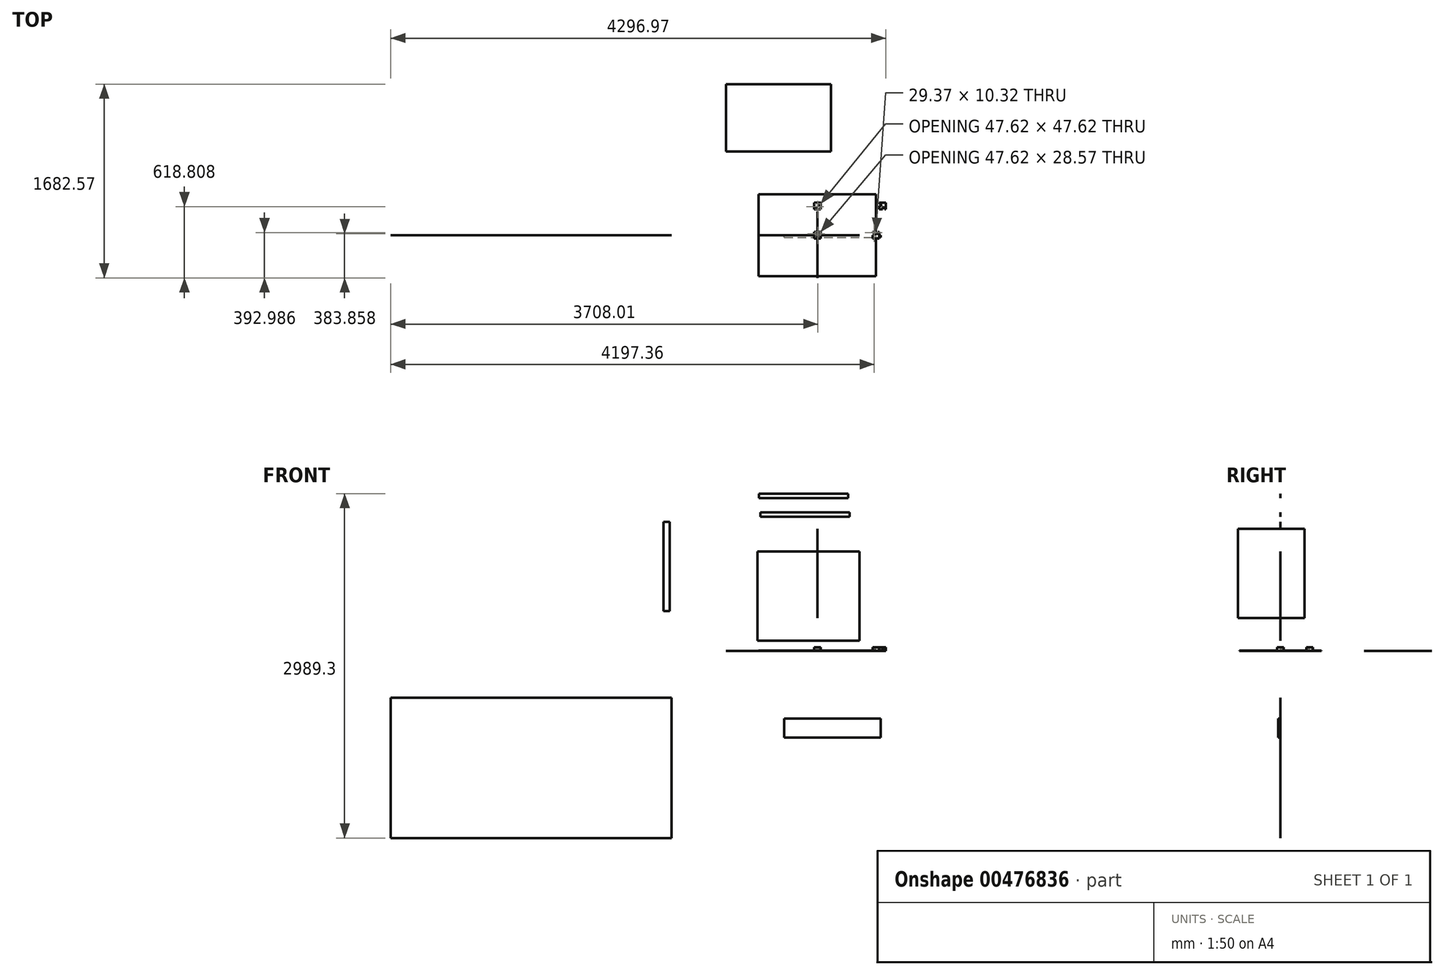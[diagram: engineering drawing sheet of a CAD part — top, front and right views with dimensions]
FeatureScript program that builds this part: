
annotation { "Feature Type Name" : "Feature", "Feature Type Description" : "" }
export const myFeature = defineFeature(function(context is Context, id is Id, definition is map)
    precondition{}
    {
        {
            assignVariable(context, id + "F0", {"name" : "h_total", "anyValue" : 36});
        }
        {
            assignVariable(context, id + "F1", {"name" : "h_caster", "anyValue" : 4});
        }
        {
            assignVariable(context, id + "F2", {"name" : "t_panel", "anyValue" : 0.72});
        }
        {
            assignVariable(context, id + "F3", {"name" : "t_top", "anyValue" : 1.5});
        }
        {
            assignVariable(context, id + "F4", {"name" : "h_panel", "anyValue" : getVariable(context, 'h_total') - getVariable(context, 'h_caster') - getVariable(context, 't_top')});
        }
        {
            var Q0;
            Q0=qCreatedBy(makeId("Top.planeOp"),FACE);
            var sketch = newSketch(context, id + "F5", { "sketchPlane" : qUnion([Q0])});
            skLineSegment(sketch, "E0.bottom", {"start": v(509.59, -355.6) * mm, "end": v(-509.59, -355.6) * mm});
            skLineSegment(sketch, "E0.top", {"start": v(509.59, 355.6) * mm, "end": v(-509.59, 355.6) * mm});
            skLineSegment(sketch, "E0.left", {"start": v(509.59, -355.6) * mm, "end": v(509.59, 355.6) * mm});
            skLineSegment(sketch, "E0.right", {"start": v(-509.59, -355.6) * mm, "end": v(-509.59, 355.6) * mm});
            skPoint(sketch, "E0.middle", {"position": v(0, 0) * mm});
            skSolve(sketch);
        }
        {
            var Q0;
            Q0=makeQuery(id+"F5.imprint","IMPRINT",FACE,{"disambiguationData":[TD([[makeQuery(id+"F5.imprint","IMPRINT",EDGE,{"derivedFrom":sQuery(id+"F5.wireOp",EDGE,"E0.bottom")}),-1.0]])]});
            extrude(context, id + "F6", {"entities" : qUnion([Q0]), "depth" : (getVariable(context, 't_top')) * mm});
        }
        {
            var Q0;
            Q0=qCreatedBy(makeId("Top.planeOp"),FACE);
            var sketch = newSketch(context, id + "F7", { "sketchPlane" : qUnion([Q0])});
            skLineSegment(sketch, "E1.bottom", {"start": v(-28.57, 28.58) * mm, "end": v(28.58, 28.58) * mm});
            skLineSegment(sketch, "E1.top", {"start": v(-28.58, -28.58) * mm, "end": v(28.58, -28.58) * mm});
            skLineSegment(sketch, "E1.left", {"start": v(-28.57, 28.58) * mm, "end": v(-28.58, -28.58) * mm});
            skLineSegment(sketch, "E1.right", {"start": v(28.58, 28.57) * mm, "end": v(28.58, -28.58) * mm});
            skPoint(sketch, "E1.middle", {"position": v(0, 0) * mm});
            skSolve(sketch);
        }
        {
            assignVariable(context, id + "F8", {"name" : "h_leg", "anyValue" : getVariable(context, 'h_panel')});
        }
        {
            var Q0;
            Q0=makeQuery(id+"F7.imprint","IMPRINT",FACE,{"disambiguationData":[TD([[makeQuery(id+"F7.imprint","IMPRINT",EDGE,{"derivedFrom":sQuery(id+"F7.wireOp",EDGE,"E1.bottom")}),-1.0]])]});
            extrude(context, id + "F9", {"entities" : qUnion([Q0]), "depth" : (getVariable(context, 'h_leg')) * mm});
        }
        {
            var Q0;
            Q0=makeQuery(id+"F9.opExtrude","SWEPT_BODY",BODY,{"disambiguationData":[OSD([sQuery(id+"F7.wireOp",EDGE,"E1.bottom"),sQuery(id+"F7.wireOp",EDGE,"E1.top"),sQuery(id+"F7.wireOp",EDGE,"E1.left"),sQuery(id+"F7.wireOp",EDGE,"E1.right")])]});
            transform(context, id + "F10", {"entities" : qUnion([Q0]), "transformType" : TransformType.TRANSLATION_3D, "dx" : 0 * mm, "dy" : 254 * mm, "dz" : 0 * mm, "makeCopy" : true});
        }
        {
            var Q0;
            Q0=makeQuery(id+"F9.opExtrude","SWEPT_BODY",BODY,{"disambiguationData":[OSD([sQuery(id+"F7.wireOp",EDGE,"E1.bottom"),sQuery(id+"F7.wireOp",EDGE,"E1.top"),sQuery(id+"F7.wireOp",EDGE,"E1.left"),sQuery(id+"F7.wireOp",EDGE,"E1.right")])]});
            transform(context, id + "F11", {"entities" : qUnion([Q0]), "transformType" : TransformType.TRANSLATION_3D, "dx" : 254 * mm, "dy" : 0 * mm, "dz" : 0 * mm, "makeCopy" : true});
        }
        {
            var Q0;
            Q0=makeQuery(id+"F10.opPattern","COPY",FACE,{"derivedFrom":makeQuery(id+"F9.opExtrude","CAP_FACE",FACE,{"disambiguationData":[OSD([sQuery(id+"F7.wireOp",EDGE,"E1.bottom"),sQuery(id+"F7.wireOp",EDGE,"E1.top"),sQuery(id+"F7.wireOp",EDGE,"E1.left"),sQuery(id+"F7.wireOp",EDGE,"E1.right")])],"isStart":false}),"instanceName":"1"});
            var sketch = newSketch(context, id + "F12", { "sketchPlane" : qUnion([Q0])});
            skLineSegment(sketch, "E2.bottom", {"start": v(28.58, 273.05) * mm, "end": v(12.7, 273.05) * mm});
            skLineSegment(sketch, "E2.top", {"start": v(28.58, 254.8) * mm, "end": v(12.7, 254.8) * mm});
            skLineSegment(sketch, "E2.left", {"start": v(28.58, 273.05) * mm, "end": v(28.58, 254.8) * mm});
            skLineSegment(sketch, "E2.right", {"start": v(12.7, 273.05) * mm, "end": v(12.7, 254.8) * mm});
            skLineSegment(sketch, "E3.bottom", {"start": v(-19.05, 225.42) * mm, "end": v(-0.8, 225.42) * mm});
            skLineSegment(sketch, "E3.top", {"start": v(-19.05, 241.3) * mm, "end": v(-0.8, 241.3) * mm});
            skLineSegment(sketch, "E3.left", {"start": v(-19.05, 225.42) * mm, "end": v(-19.05, 241.3) * mm});
            skLineSegment(sketch, "E3.right", {"start": v(-0.8, 225.42) * mm, "end": v(-0.8, 241.3) * mm});
            skSolve(sketch);
        }
        {
            var Q0;
            Q0=makeQuery(id+"F12.imprint","IMPRINT",FACE,{"disambiguationData":[TD([[makeQuery(id+"F12.imprint","IMPRINT",EDGE,{"derivedFrom":sQuery(id+"F12.wireOp",EDGE,"E3.bottom")}),1.0]])]});
            var Q1;
            Q1=makeQuery(id+"F12.imprint","IMPRINT",FACE,{"disambiguationData":[TD([[makeQuery(id+"F12.imprint","IMPRINT",EDGE,{"derivedFrom":sQuery(id+"F12.wireOp",EDGE,"E2.bottom")}),1.0]])]});
            extrude(context, id + "F13", {"entities" : qUnion([Q0, Q1]), "operationType" : NewBodyOperationType.REMOVE, "endBound" : BoundingType.THROUGH_ALL, "oppositeDirection" : true, "depth" : 25.4 * mm});
        }
        {
            var Q0;
            Q0=makeQuery(id+"F10.opPattern","COPY",BODY,{"derivedFrom":makeQuery(id+"F9.opExtrude","SWEPT_BODY",BODY,{"disambiguationData":[OSD([sQuery(id+"F7.wireOp",EDGE,"E1.bottom"),sQuery(id+"F7.wireOp",EDGE,"E1.top"),sQuery(id+"F7.wireOp",EDGE,"E1.left"),sQuery(id+"F7.wireOp",EDGE,"E1.right")])]}),"instanceName":"1"});
            var Q1;
            Q1=makeQuery(id+"F11.opPattern","COPY",FACE,{"derivedFrom":makeQuery(id+"F9.opExtrude","SWEPT_FACE",FACE,{"disambiguationData":[OSD([sQuery(id+"F7.wireOp",EDGE,"E1.right")])]}),"instanceName":"1"});
            mirror(context, id + "F14", {"entities" : qUnion([Q0]), "mirrorPlane" : qUnion([Q1])});
        }
        {
            var Q0;
            Q0=makeQuery(id+"F11.opPattern","COPY",BODY,{"derivedFrom":makeQuery(id+"F9.opExtrude","SWEPT_BODY",BODY,{"disambiguationData":[OSD([sQuery(id+"F7.wireOp",EDGE,"E1.bottom"),sQuery(id+"F7.wireOp",EDGE,"E1.top"),sQuery(id+"F7.wireOp",EDGE,"E1.left"),sQuery(id+"F7.wireOp",EDGE,"E1.right")])]}),"instanceName":"1"});
            deleteBodies(context, id + "F15", {"entities" : qUnion([Q0])});
        }
        {
            var Q0;
            Q0=qCreatedBy(makeId("Right.planeOp"),FACE);
            cPlane(context, id + "F16", {"entities" : qUnion([Q0]), "cplaneType" : CPlaneType.OFFSET, "offset" : 254 * mm, "width" : 152.4 * mm, "height" : 152.4 * mm});
        }
        {
            var Q0;
            Q0=makeQuery(id+"F9.opExtrude","CAP_FACE",FACE,{"disambiguationData":[OSD([sQuery(id+"F7.wireOp",EDGE,"E1.bottom"),sQuery(id+"F7.wireOp",EDGE,"E1.top"),sQuery(id+"F7.wireOp",EDGE,"E1.left"),sQuery(id+"F7.wireOp",EDGE,"E1.right")])],"isStart":false});
            var sketch = newSketch(context, id + "F17", { "sketchPlane" : qUnion([Q0])});
            skLineSegment(sketch, "E4.bottom", {"start": v(28.58, 0) * mm, "end": v(12.7, 0) * mm});
            skLineSegment(sketch, "E4.top", {"start": v(28.58, 18.26) * mm, "end": v(12.7, 18.26) * mm});
            skLineSegment(sketch, "E4.left", {"start": v(28.58, 0) * mm, "end": v(28.58, 18.26) * mm});
            skLineSegment(sketch, "E4.right", {"start": v(12.7, 0) * mm, "end": v(12.7, 18.26) * mm});
            skLineSegment(sketch, "E5.bottom", {"start": v(-19.05, 28.58) * mm, "end": v(-0.8, 28.58) * mm});
            skLineSegment(sketch, "E5.top", {"start": v(-19.05, 12.7) * mm, "end": v(-0.8, 12.7) * mm});
            skLineSegment(sketch, "E5.left", {"start": v(-19.05, 28.58) * mm, "end": v(-19.05, 12.7) * mm});
            skLineSegment(sketch, "E5.right", {"start": v(-0.8, 28.58) * mm, "end": v(-0.8, 12.7) * mm});
            skSolve(sketch);
        }
        {
            var Q0;
            Q0=makeQuery(id+"F17.imprint","IMPRINT",FACE,{"disambiguationData":[TD([[makeQuery(id+"F17.imprint","IMPRINT",EDGE,{"derivedFrom":sQuery(id+"F17.wireOp",EDGE,"E5.bottom")}),-1.0]])]});
            var Q1;
            Q1=makeQuery(id+"F17.imprint","IMPRINT",FACE,{"disambiguationData":[TD([[makeQuery(id+"F17.imprint","IMPRINT",EDGE,{"derivedFrom":sQuery(id+"F17.wireOp",EDGE,"E4.bottom")}),-1.0]])]});
            extrude(context, id + "F18", {"entities" : qUnion([Q0, Q1]), "operationType" : NewBodyOperationType.REMOVE, "endBound" : BoundingType.THROUGH_ALL, "oppositeDirection" : true, "depth" : 25.4 * mm});
        }
        {
            var Q0;
            Q0=makeQuery(id+"F9.opExtrude","SWEPT_BODY",BODY,{"disambiguationData":[OSD([sQuery(id+"F7.wireOp",EDGE,"E1.bottom"),sQuery(id+"F7.wireOp",EDGE,"E1.top"),sQuery(id+"F7.wireOp",EDGE,"E1.left"),sQuery(id+"F7.wireOp",EDGE,"E1.right")])]});
            var Q1;
            Q1=qCreatedBy(id+"F16.planeOp",FACE);
            mirror(context, id + "F19", {"entities" : qUnion([Q0]), "mirrorPlane" : qUnion([Q1])});
        }
        {
            var Q0;
            Q0=qCreatedBy(makeId("Front.planeOp"),FACE);
            var sketch = newSketch(context, id + "F20", { "sketchPlane" : qUnion([Q0])});
            skLineSegment(sketch, "E6.bottom", {"start": v(-520.64, 864.35) * mm, "end": v(365.19, 864.35) * mm});
            skLineSegment(sketch, "E6.top", {"start": v(-520.64, 89.65) * mm, "end": v(365.19, 89.65) * mm});
            skLineSegment(sketch, "E6.left", {"start": v(-520.64, 864.35) * mm, "end": v(-520.64, 89.65) * mm});
            skLineSegment(sketch, "E6.right", {"start": v(365.19, 864.35) * mm, "end": v(365.19, 89.65) * mm});
            skSolve(sketch);
        }
        {
            var Q0;
            Q0=makeQuery(id+"F20.imprint","IMPRINT",FACE,{"disambiguationData":[TD([[makeQuery(id+"F20.imprint","IMPRINT",EDGE,{"derivedFrom":sQuery(id+"F20.wireOp",EDGE,"E6.bottom")}),-1.0]])]});
            extrude(context, id + "F21", {"entities" : qUnion([Q0]), "depth" : (getVariable(context, 't_panel')) * mm});
        }
        {
            var Q0;
            Q0=qCreatedBy(makeId("Right.planeOp"),FACE);
            var sketch = newSketch(context, id + "F22", { "sketchPlane" : qUnion([Q0])});
            skLineSegment(sketch, "E7.bottom", {"start": v(-369.57, 1058.76) * mm, "end": v(208.28, 1058.76) * mm});
            skLineSegment(sketch, "E7.top", {"start": v(-369.57, 284.06) * mm, "end": v(208.28, 284.06) * mm});
            skLineSegment(sketch, "E7.left", {"start": v(-369.57, 1058.76) * mm, "end": v(-369.57, 284.06) * mm});
            skLineSegment(sketch, "E7.right", {"start": v(208.28, 1058.76) * mm, "end": v(208.28, 284.06) * mm});
            skSolve(sketch);
        }
        {
            var Q0;
            Q0=makeQuery(id+"F22.imprint","IMPRINT",FACE,{"disambiguationData":[TD([[makeQuery(id+"F22.imprint","IMPRINT",EDGE,{"derivedFrom":sQuery(id+"F22.wireOp",EDGE,"E7.bottom")}),-1.0]])]});
            extrude(context, id + "F23", {"entities" : qUnion([Q0]), "depth" : (getVariable(context, 't_panel')) * mm});
        }
        {
            assignVariable(context, id + "F24", {"name" : "w_stile", "anyValue" : 1.5});
        }
        {
            var Q0;
            Q0=qCreatedBy(makeId("Front.planeOp"),FACE);
            var sketch = newSketch(context, id + "F25", { "sketchPlane" : qUnion([Q0])});
            skLineSegment(sketch, "E8.bottom", {"start": v(-506.03, 1326.18) * mm, "end": v(268.67, 1326.18) * mm});
            skLineSegment(sketch, "E8.top", {"start": v(-506.03, 1364.28) * mm, "end": v(268.67, 1364.28) * mm});
            skLineSegment(sketch, "E8.left", {"start": v(-506.03, 1326.18) * mm, "end": v(-506.03, 1364.28) * mm});
            skLineSegment(sketch, "E8.right", {"start": v(268.67, 1326.18) * mm, "end": v(268.67, 1364.28) * mm});
            skSolve(sketch);
        }
        {
            var Q0;
            Q0 = qSketchRegion(id + "F25", true);
            extrude(context, id + "F26", {"entities" : qUnion([Q0]), "depth" : (getVariable(context, 't_panel')) * mm, "offsetDistance" : 25.4 * mm});
        }
        {
            var Q0;
            Q0=qCreatedBy(makeId("Front.planeOp"),FACE);
            var sketch = newSketch(context, id + "F27", { "sketchPlane" : qUnion([Q0])});
            skLineSegment(sketch, "E9.bottom", {"start": v(-1336.14, 1121.53) * mm, "end": v(-1280.58, 1121.53) * mm});
            skLineSegment(sketch, "E9.top", {"start": v(-1336.14, 346.83) * mm, "end": v(-1280.58, 346.83) * mm});
            skLineSegment(sketch, "E9.left", {"start": v(-1336.14, 1121.53) * mm, "end": v(-1336.14, 346.83) * mm});
            skLineSegment(sketch, "E9.right", {"start": v(-1280.58, 1121.53) * mm, "end": v(-1280.58, 346.83) * mm});
            skSolve(sketch);
        }
        {
            var Q0;
            Q0=makeQuery(id+"F27.imprint","IMPRINT",FACE,{"disambiguationData":[TD([[makeQuery(id+"F27.imprint","IMPRINT",EDGE,{"derivedFrom":sQuery(id+"F27.wireOp",EDGE,"E9.bottom")}),-1.0]])]});
            extrude(context, id + "F28", {"entities" : qUnion([Q0]), "depth" : (getVariable(context, 't_panel')) * mm, "offsetDistance" : 25.4 * mm});
        }
        {
            var Q0;
            Q0=makeQuery(id+"F26.opExtrude","SWEPT_BODY",BODY,{"disambiguationData":[OSD([sQuery(id+"F25.wireOp",EDGE,"E8.bottom"),sQuery(id+"F25.wireOp",EDGE,"E8.top"),sQuery(id+"F25.wireOp",EDGE,"E8.left"),sQuery(id+"F25.wireOp",EDGE,"E8.right")])]});
            transform(context, id + "F29", {"entities" : qUnion([Q0]), "transformType" : TransformType.TRANSLATION_3D, "dx" : 0 * mm, "dy" : 0 * mm, "dz" : 127 * mm, "makeCopy" : true});
        }
        {
            var Q0;
            Q0=makeQuery(id+"F29.opPattern","COPY",BODY,{"derivedFrom":makeQuery(id+"F26.opExtrude","SWEPT_BODY",BODY,{"disambiguationData":[OSD([sQuery(id+"F25.wireOp",EDGE,"E8.bottom"),sQuery(id+"F25.wireOp",EDGE,"E8.top"),sQuery(id+"F25.wireOp",EDGE,"E8.left"),sQuery(id+"F25.wireOp",EDGE,"E8.right")])]}),"instanceName":"1"});
            deleteBodies(context, id + "F30", {"entities" : qUnion([Q0])});
        }
        {
            var Q0;
            Q0=qCreatedBy(makeId("Front.planeOp"),FACE);
            var sketch = newSketch(context, id + "F31", { "sketchPlane" : qUnion([Q0])});
            skLineSegment(sketch, "E10.bottom", {"start": v(-493.85, 1164.48) * mm, "end": v(280.85, 1164.48) * mm});
            skLineSegment(sketch, "E10.top", {"start": v(-493.85, 1202.58) * mm, "end": v(280.85, 1202.58) * mm});
            skLineSegment(sketch, "E10.left", {"start": v(-493.85, 1164.48) * mm, "end": v(-493.85, 1202.58) * mm});
            skLineSegment(sketch, "E10.right", {"start": v(280.85, 1164.48) * mm, "end": v(280.85, 1202.58) * mm});
            skSolve(sketch);
        }
        {
            var Q0;
            Q0=makeQuery(id+"F31.imprint","IMPRINT",FACE,{"disambiguationData":[TD([[makeQuery(id+"F31.imprint","IMPRINT",EDGE,{"derivedFrom":sQuery(id+"F31.wireOp",EDGE,"E10.bottom")}),1.0]])]});
            extrude(context, id + "F32", {"entities" : qUnion([Q0]), "depth" : (getVariable(context, 't_panel')) * mm, "offsetDistance" : 25.4 * mm});
        }
        {
            assignVariable(context, id + "F33", {"name" : "d_bottom", "anyValue" : getVariable(context, 'w_stile')});
        }
        {
            var Q0;
            Q0=makeQuery(id+"F10.opPattern","COPY",FACE,{"derivedFrom":makeQuery(id+"F9.opExtrude","CAP_FACE",FACE,{"disambiguationData":[OSD([sQuery(id+"F7.wireOp",EDGE,"E1.bottom"),sQuery(id+"F7.wireOp",EDGE,"E1.top"),sQuery(id+"F7.wireOp",EDGE,"E1.left"),sQuery(id+"F7.wireOp",EDGE,"E1.right")])],"isStart":true}),"instanceName":"1"});
            var sketch = newSketch(context, id + "F34", { "sketchPlane" : qUnion([Q0])});
            skLineSegment(sketch, "E11.bottom", {"start": v(-0.8, -225.42) * mm, "end": v(28.58, -225.42) * mm});
            skLineSegment(sketch, "E11.top", {"start": v(-0.8, -254.8) * mm, "end": v(28.58, -254.8) * mm});
            skLineSegment(sketch, "E11.left", {"start": v(-0.8, -225.42) * mm, "end": v(-0.8, -254.8) * mm});
            skLineSegment(sketch, "E11.right", {"start": v(28.58, -225.42) * mm, "end": v(28.58, -254.8) * mm});
            skSolve(sketch);
        }
        {
            var Q0;
            {var subQ3=sQuery(id+"F34.wireOp",EDGE,"E11.bottom");Q0=makeQuery(id+"F34.imprint","IMPRINT",FACE,{"disambiguationData":[TD([[makeQuery(id+"F34.imprint","IMPRINT",EDGE,{"derivedFrom":subQ3}),-1.0]])]});}
            extrude(context, id + "F35", {"entities" : qUnion([Q0]), "operationType" : NewBodyOperationType.REMOVE, "oppositeDirection" : true, "depth" : (getVariable(context, 'd_bottom')) * mm, "offsetDistance" : 25.4 * mm});
        }
        {
            var Q0;
            Q0=makeQuery(id+"F14.opPattern","COPY",FACE,{"derivedFrom":makeQuery(id+"F10.opPattern","COPY",FACE,{"derivedFrom":makeQuery(id+"F9.opExtrude","CAP_FACE",FACE,{"disambiguationData":[OSD([sQuery(id+"F7.wireOp",EDGE,"E1.bottom"),sQuery(id+"F7.wireOp",EDGE,"E1.top"),sQuery(id+"F7.wireOp",EDGE,"E1.left"),sQuery(id+"F7.wireOp",EDGE,"E1.right")])],"isStart":true}),"instanceName":"1"}),"instanceName":"1"});
            var sketch = newSketch(context, id + "F36", { "sketchPlane" : qUnion([Q0])});
            skLineSegment(sketch, "E12.bottom", {"start": v(536.58, -254.8) * mm, "end": v(565.94, -254.8) * mm});
            skLineSegment(sketch, "E12.top", {"start": v(536.58, -225.42) * mm, "end": v(565.94, -225.42) * mm});
            skLineSegment(sketch, "E12.left", {"start": v(536.58, -254.8) * mm, "end": v(536.58, -225.42) * mm});
            skLineSegment(sketch, "E12.right", {"start": v(565.94, -254.8) * mm, "end": v(565.94, -225.42) * mm});
            skSolve(sketch);
        }
        {
            var Q0;
            {var subQ1=sQuery(id+"F36.wireOp",EDGE,"E12.top");Q0=makeQuery(id+"F36.imprint","IMPRINT",FACE,{"disambiguationData":[TD([[makeQuery(id+"F36.imprint","IMPRINT",EDGE,{"derivedFrom":subQ1}),1.0]])]});}
            extrude(context, id + "F37", {"entities" : qUnion([Q0]), "operationType" : NewBodyOperationType.REMOVE, "oppositeDirection" : true, "depth" : (getVariable(context, 'd_bottom')) * mm, "offsetDistance" : 25.4 * mm});
        }
        {
            var Q0;
            Q0=makeQuery(id+"F19.opPattern","COPY",FACE,{"derivedFrom":makeQuery(id+"F9.opExtrude","CAP_FACE",FACE,{"disambiguationData":[OSD([sQuery(id+"F7.wireOp",EDGE,"E1.bottom"),sQuery(id+"F7.wireOp",EDGE,"E1.top"),sQuery(id+"F7.wireOp",EDGE,"E1.left"),sQuery(id+"F7.wireOp",EDGE,"E1.right")])],"isStart":true}),"instanceName":"1"});
            var sketch = newSketch(context, id + "F38", { "sketchPlane" : qUnion([Q0])});
            skLineSegment(sketch, "E13.bottom", {"start": v(479.43, -18.26) * mm, "end": v(508.8, -18.26) * mm});
            skLineSegment(sketch, "E13.top", {"start": v(479.43, -28.58) * mm, "end": v(508.8, -28.58) * mm});
            skLineSegment(sketch, "E13.left", {"start": v(479.43, -18.26) * mm, "end": v(479.43, -28.58) * mm});
            skLineSegment(sketch, "E13.right", {"start": v(508.8, -18.26) * mm, "end": v(508.8, -28.58) * mm});
            skSolve(sketch);
        }
        {
            var Q0;
            Q0=makeQuery(id+"F38.imprint","IMPRINT",FACE,{"disambiguationData":[TD([[makeQuery(id+"F38.imprint","IMPRINT",EDGE,{"derivedFrom":sQuery(id+"F38.wireOp",EDGE,"E13.top")}),-1.0]])]});
            extrude(context, id + "F39", {"entities" : qUnion([Q0]), "operationType" : NewBodyOperationType.REMOVE, "oppositeDirection" : true, "depth" : (getVariable(context, 'd_bottom')) * mm, "offsetDistance" : 25.4 * mm});
        }
        {
            var Q0;
            Q0=makeQuery(id+"F9.opExtrude","CAP_FACE",FACE,{"disambiguationData":[OSD([sQuery(id+"F7.wireOp",EDGE,"E1.bottom"),sQuery(id+"F7.wireOp",EDGE,"E1.top"),sQuery(id+"F7.wireOp",EDGE,"E1.left"),sQuery(id+"F7.wireOp",EDGE,"E1.right")])],"isStart":true});
            var sketch = newSketch(context, id + "F40", { "sketchPlane" : qUnion([Q0])});
            skLineSegment(sketch, "E14.bottom", {"start": v(28.58, -18.26) * mm, "end": v(-0.8, -18.26) * mm});
            skLineSegment(sketch, "E14.top", {"start": v(28.58, -28.58) * mm, "end": v(-0.8, -28.58) * mm});
            skLineSegment(sketch, "E14.left", {"start": v(28.58, -18.26) * mm, "end": v(28.58, -28.58) * mm});
            skLineSegment(sketch, "E14.right", {"start": v(-0.8, -18.26) * mm, "end": v(-0.8, -28.58) * mm});
            skSolve(sketch);
        }
        {
            var Q0;
            Q0=makeQuery(id+"F40.imprint","IMPRINT",FACE,{"disambiguationData":[TD([[makeQuery(id+"F40.imprint","IMPRINT",EDGE,{"derivedFrom":sQuery(id+"F40.wireOp",EDGE,"E14.top")}),1.0]])]});
            extrude(context, id + "F41", {"entities" : qUnion([Q0]), "operationType" : NewBodyOperationType.REMOVE, "oppositeDirection" : true, "depth" : (getVariable(context, 'd_bottom')) * mm, "offsetDistance" : 25.4 * mm});
        }
        {
            var Q0;
            Q0=qCreatedBy(makeId("Top.planeOp"),FACE);
            var sketch = newSketch(context, id + "F42", { "sketchPlane" : qUnion([Q0])});
            skLineSegment(sketch, "E15.bottom", {"start": v(-794.25, 1313) * mm, "end": v(118.56, 1313) * mm});
            skLineSegment(sketch, "E15.top", {"start": v(-794.25, 727.21) * mm, "end": v(118.56, 727.21) * mm});
            skLineSegment(sketch, "E15.left", {"start": v(-794.25, 1313) * mm, "end": v(-794.25, 727.21) * mm});
            skLineSegment(sketch, "E15.right", {"start": v(118.56, 1313) * mm, "end": v(118.56, 727.21) * mm});
            skSolve(sketch);
        }
        {
            var Q0;
            Q0=makeQuery(id+"F42.imprint","IMPRINT",FACE,{"disambiguationData":[TD([[makeQuery(id+"F42.imprint","IMPRINT",EDGE,{"derivedFrom":sQuery(id+"F42.wireOp",EDGE,"E15.bottom")}),-1.0]])]});
            extrude(context, id + "F43", {"entities" : qUnion([Q0]), "depth" : (getVariable(context, 't_panel')) * mm, "offsetDistance" : 25.4 * mm});
        }
        {
            var Q0;
            Q0=qCreatedBy(makeId("Front.planeOp"),FACE);
            var sketch = newSketch(context, id + "F44", { "sketchPlane" : qUnion([Q0])});
            skLineSegment(sketch, "E16.bottom", {"start": v(-3703.25, -405.82) * mm, "end": v(-1264.85, -405.82) * mm});
            skLineSegment(sketch, "E16.top", {"start": v(-3703.25, -1625.02) * mm, "end": v(-1264.85, -1625.02) * mm});
            skLineSegment(sketch, "E16.left", {"start": v(-3703.25, -405.82) * mm, "end": v(-3703.25, -1625.02) * mm});
            skLineSegment(sketch, "E16.right", {"start": v(-1264.85, -405.82) * mm, "end": v(-1264.85, -1625.02) * mm});
            skSolve(sketch);
        }
        {
            var Q0;
            Q0=makeQuery(id+"F44.imprint","IMPRINT",FACE,{"disambiguationData":[TD([[makeQuery(id+"F44.imprint","IMPRINT",EDGE,{"derivedFrom":sQuery(id+"F44.wireOp",EDGE,"E16.bottom")}),-1.0]])]});
            extrude(context, id + "F45", {"entities" : qUnion([Q0]), "depth" : (getVariable(context, 't_panel')) * mm, "offsetDistance" : 25.4 * mm});
        }
        {
            var Q0;
            Q0=qCreatedBy(makeId("Front.planeOp"),FACE);
            var sketch = newSketch(context, id + "F46", { "sketchPlane" : qUnion([Q0])});
            skLineSegment(sketch, "E17.bottom", {"start": v(-286.44, -753.34) * mm, "end": v(551.76, -753.34) * mm});
            skLineSegment(sketch, "E17.top", {"start": v(-286.44, -588.24) * mm, "end": v(551.76, -588.24) * mm});
            skLineSegment(sketch, "E17.left", {"start": v(-286.44, -753.34) * mm, "end": v(-286.44, -588.24) * mm});
            skLineSegment(sketch, "E17.right", {"start": v(551.76, -753.34) * mm, "end": v(551.76, -588.24) * mm});
            skSolve(sketch);
        }
        {
            var Q0;
            Q0=makeQuery(id+"F46.imprint","IMPRINT",FACE,{"disambiguationData":[TD([[makeQuery(id+"F46.imprint","IMPRINT",EDGE,{"derivedFrom":sQuery(id+"F46.wireOp",EDGE,"E17.bottom")}),1.0]])]});
            extrude(context, id + "F47", {"entities" : qUnion([Q0]), "depth" : 19.05 * mm, "offsetDistance" : 25.4 * mm});
        }
    });
